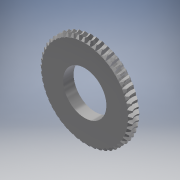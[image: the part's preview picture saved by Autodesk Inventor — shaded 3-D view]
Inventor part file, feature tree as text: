
AUTODESK INVENTOR PART (.ipt)
format: ipt  version: 2019.3 (Build 233278000, 278)  size: 1,016,832 bytes
history: native  units: mm (DEFAULTED — no unit token found)
features: other x8, plane x3, sketch x2, pattern_circular x1, extrude x1
ambient origin geometry x5: Origin, X Axis, Y Axis, Z Axis, Center Point
bodies: Solid1 (feature_tree)
feature tree (15):
  other  "Tooth Plane"
  other  "Base Body Sketch"
  other  "Base Body"
  other  "Base Body2"
  plane  "Work Plane13"
  other  "Tooth"
  pattern_circular  "Tooth Pattern"  [2 undecoded]
  plane  "Work Plane14"
  plane  "Work Plane15"
  extrude  "Extrusion1"  Depth=58.657497mm
  other  "Tooth Sketch"
  sketch  "Sketch8"  dims[d35=90.0deg]
  other  "Srf1"
  sketch  "Sketch9"  dims[d37=-1.23738mm d38=58.657497mm d39=3.490659mm d40=5.700281mm d41=8.125802mm d42=1.905mm d43=90.0deg d44=500.0mm d46=360.0deg d50=6.511309mm d68=58.657497mm d69=0.0mm d73=0.0mm d75=0.628319mm d77=101.063389mm d78=12.3mm d79=0.0mm d80=0.0mm d81=0.0mm d82=0.0mm d83=0.628319mm d84=0.0mm d85=180.0deg d86=58.657497mm d87=107.127192mm d89=12.209069mm d90=90.0deg d92=12.3mm d93=58.657497mm d94=50.546mm d95=25.4mm d96=0.0mm]
  other  "Pitch Diameter"
note: 2 required parameter values undecoded (feature->parameter linkage not recoverable at this tier; creation-order binding heuristic only, values carry confidence <= 0.55)
